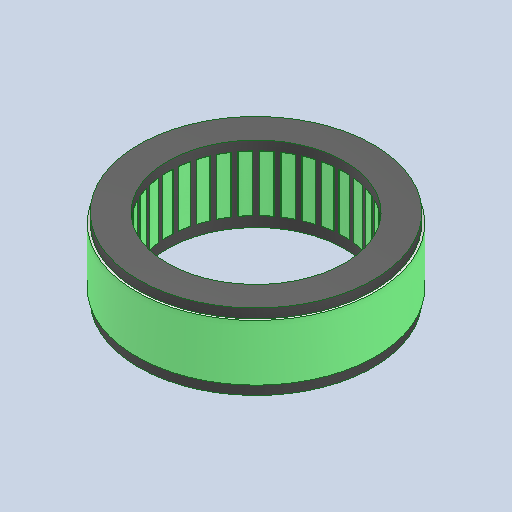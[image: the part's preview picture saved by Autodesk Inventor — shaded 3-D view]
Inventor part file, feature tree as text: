
AUTODESK INVENTOR PART (.ipt)
format: ipt  version: 2023.4 (Build 274418000, 418)  size: 247,296 bytes
history: native  units: mm
features: extrude x1
ambient origin geometry x8: Origin, YZ Plane, XZ Plane, XY Plane, X Axis, Y Axis, Z Axis, Center Point
bodies: Solid1 (feature_tree)
feature tree (1):
  extrude  "Extrude3"  [1 undecoded]
note: 1 required parameter value undecoded (feature->parameter linkage not recoverable at this tier; creation-order binding heuristic only, values carry confidence <= 0.55)
